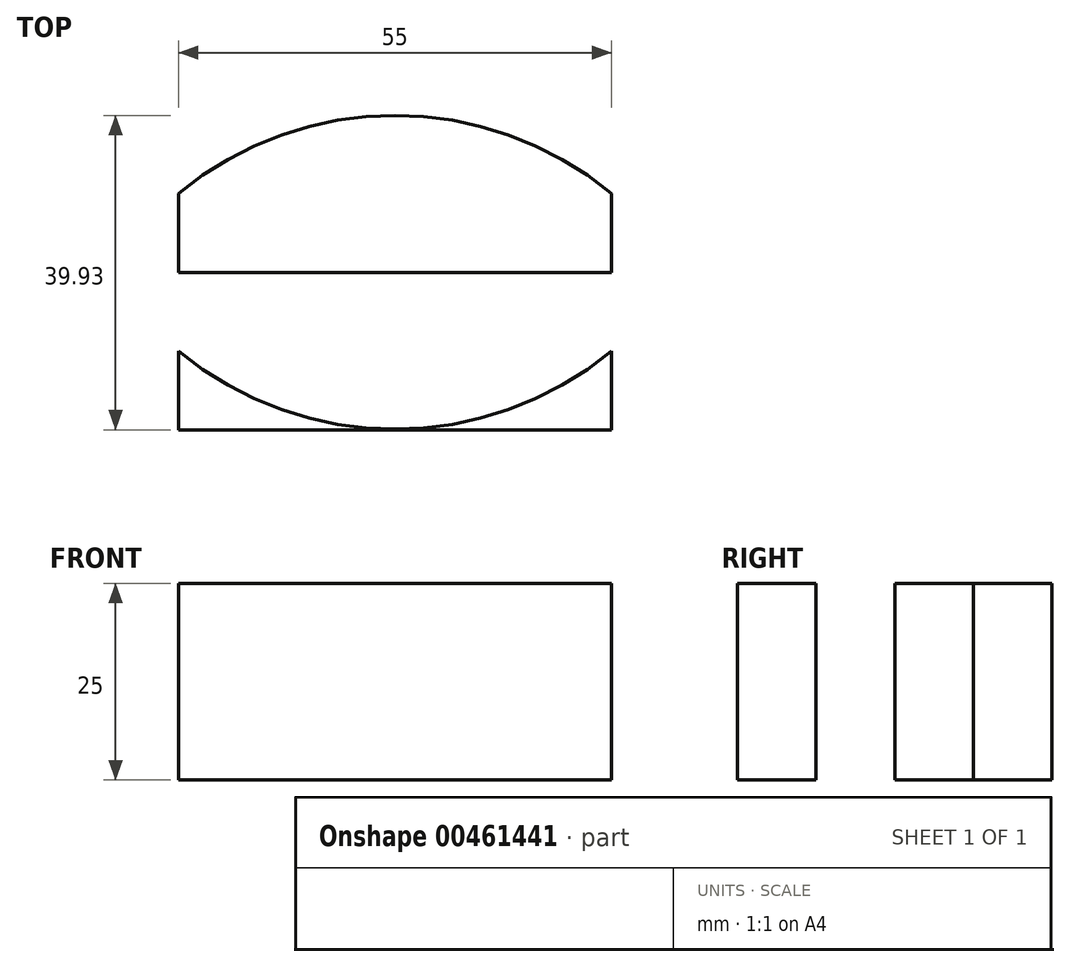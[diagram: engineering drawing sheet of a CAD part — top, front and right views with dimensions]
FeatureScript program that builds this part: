
annotation { "Feature Type Name" : "Feature", "Feature Type Description" : "" }
export const myFeature = defineFeature(function(context is Context, id is Id, definition is map)
    precondition{}
    {
        {
            var Q0;
            Q0=qCreatedBy(makeId("Top.planeOp"),FACE);
            var sketch = newSketch(context, id + "F0", { "sketchPlane" : qUnion([Q0])});
            skLineSegment(sketch, "E0.bottom", {"start": v(0, 0) * mm, "end": v(55, 0) * mm});
            skLineSegment(sketch, "E0.top", {"start": v(0, -40) * mm, "end": v(55, -40) * mm});
            skLineSegment(sketch, "E0.left", {"start": v(0, 0) * mm, "end": v(0, -40) * mm});
            skLineSegment(sketch, "E0.right", {"start": v(55, 0) * mm, "end": v(55, -40) * mm});
            skSolve(sketch);
        }
        {
            var Q0;
            Q0 = qSketchRegion(id + "F0", true);
            extrude(context, id + "F1", {"entities" : qUnion([Q0]), "depth" : 25 * mm});
        }
        {
            var Q0;
            Q0=makeQuery(id+"F1.opExtrude","CAP_FACE",FACE,{"disambiguationData":[OSD([sQuery(id+"F0.wireOp",EDGE,"E0.bottom"),sQuery(id+"F0.wireOp",EDGE,"E0.top"),sQuery(id+"F0.wireOp",EDGE,"E0.left"),sQuery(id+"F0.wireOp",EDGE,"E0.right")])],"isStart":false});
            var sketch = newSketch(context, id + "F2", { "sketchPlane" : qUnion([Q0])});
            skLineSegment(sketch, "E1", {"start": v(0, 0) * mm, "end": v(0, -20) * mm});
            skLineSegment(sketch, "E2", {"start": v(0, -20) * mm, "end": v(55, -20) * mm});
            skArc(sketch, "E3", {"start": v(55, -10) * mm, "mid": v(27.5, -0.07) * mm, "end": v(0, -10) * mm});
            skPoint(sketch, "E3.startSnap0", {"position": v(0, -10) * mm});
            skArc(sketch, "E4.MirrorCS", {"start": v(55, -30) * mm, "mid": v(27.5, -39.93) * mm, "end": v(0, -30) * mm});
            skSolve(sketch);
        }
        {
            var Q0;
            {var subQ2=sQuery(id+"F2.wireOp",EDGE,"E3");Q0=makeQuery(id+"F2.imprint","IMPRINT",FACE,{"disambiguationData":[TD([[makeQuery(id+"F2.imprint","IMPRINT",EDGE,{"derivedFrom":subQ2}),-1.0]])]});}
            var Q1;
            {var subQ0=sQuery(id+"F2.wireOp",EDGE,"E4.MirrorCS");Q1=makeQuery(id+"F2.imprint","IMPRINT",FACE,{"disambiguationData":[TD([[makeQuery(id+"F2.imprint","IMPRINT",EDGE,{"derivedFrom":subQ0}),1.0]])]});}
            extrude(context, id + "F3", {"entities" : qUnion([Q0, Q1]), "operationType" : NewBodyOperationType.REMOVE, "oppositeDirection" : true, "depth" : 25 * mm});
        }
    });
